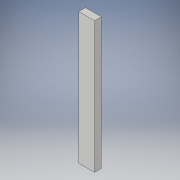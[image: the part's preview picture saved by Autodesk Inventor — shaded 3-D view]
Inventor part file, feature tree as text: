
AUTODESK INVENTOR PART (.ipt)
format: ipt  version: 2017 (Build 210142000, 142)  size: 92,160 bytes
history: native  units: in
note: dims shown in document units (in); Inventor stores cm internally (conversion verified against a paired STEP export)
features: extrude x1, sketch x1
ambient origin geometry x8: Origin, YZ Plane, XZ Plane, XY Plane, X Axis, Y Axis, Z Axis, Center Point
bodies: Solid1 (feature_tree)
feature tree (2):
  extrude  "Extrusion1"  Depth=1.5in
  sketch  "Sketch1"  dims[d0=3.5in d1=1.5in d2=29.0in d3=0.0in]
